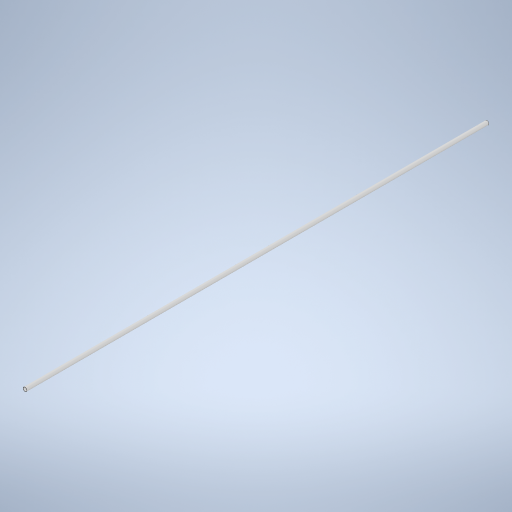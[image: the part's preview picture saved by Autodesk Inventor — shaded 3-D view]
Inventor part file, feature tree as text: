
AUTODESK INVENTOR PART (.ipt)
format: ipt  version: 2023 (Build 270158000, 158)  size: 237,056 bytes
history: native  units: mm
features: extrude x1, sketch x1
ambient origin geometry x8: Origin, YZ Plane, XZ Plane, XY Plane, X Axis, Y Axis, Z Axis, Center Point
bodies: Solido1 (feature_tree)
feature tree (2):
  extrude  "Estrusione1"  Depth=50.0mm
  sketch  "Schizzo1"
